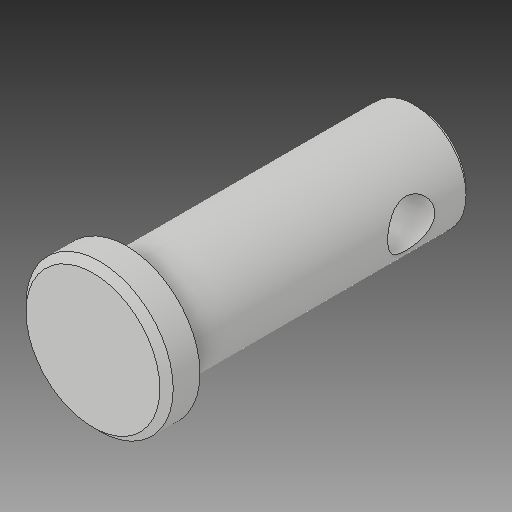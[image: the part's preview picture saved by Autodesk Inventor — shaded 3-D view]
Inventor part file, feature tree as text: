
AUTODESK INVENTOR PART (.ipt)
format: ipt  version: 2017 (Build 210142000, 142)  size: 122,880 bytes
history: native  units: mm
features: chamfer x1
ambient origin geometry x8: Origin, YZ Plane, XZ Plane, XY Plane, X Axis, Y Axis, Z Axis, Center Point
bodies: Solid1 (feature_tree)
feature tree (1):
  chamfer  "Chamfer2"  [1 undecoded]
note: 1 required parameter value undecoded (feature->parameter linkage not recoverable at this tier; creation-order binding heuristic only, values carry confidence <= 0.55)
